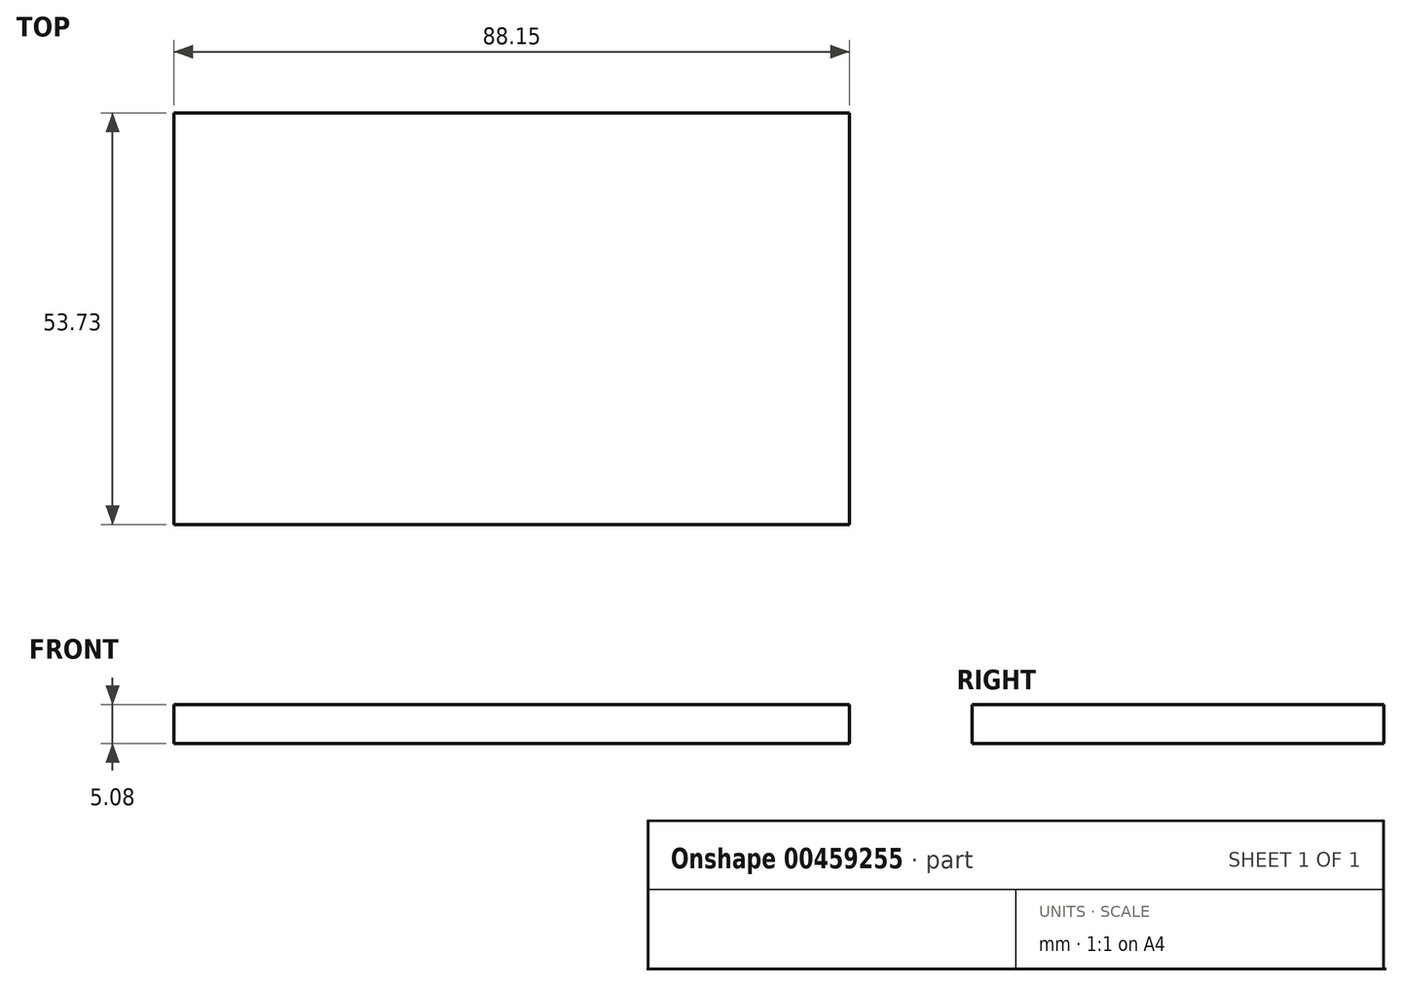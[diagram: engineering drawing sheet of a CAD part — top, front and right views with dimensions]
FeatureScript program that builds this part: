
annotation { "Feature Type Name" : "Feature", "Feature Type Description" : "" }
export const myFeature = defineFeature(function(context is Context, id is Id, definition is map)
    precondition{}
    {
        {
            var Q0;
            Q0=qCreatedBy(makeId("Top.planeOp"),FACE);
            var sketch = newSketch(context, id + "F0", { "sketchPlane" : qUnion([Q0])});
            skLineSegment(sketch, "E0.bottom", {"start": v(-24.19, 15.82) * mm, "end": v(63.96, 15.82) * mm});
            skLineSegment(sketch, "E0.top", {"start": v(-24.19, -37.91) * mm, "end": v(63.96, -37.91) * mm});
            skLineSegment(sketch, "E0.left", {"start": v(-24.19, 15.82) * mm, "end": v(-24.19, -37.91) * mm});
            skLineSegment(sketch, "E0.right", {"start": v(63.96, 15.82) * mm, "end": v(63.96, -37.91) * mm});
            skSolve(sketch);
        }
        {
            var Q0;
            Q0=makeQuery(id+"F0.imprint","IMPRINT",FACE,{"disambiguationData":[TD([[makeQuery(id+"F0.imprint","IMPRINT",EDGE,{"derivedFrom":sQuery(id+"F0.wireOp",EDGE,"E0.bottom")}),-1.0]])]});
            extrude(context, id + "F1", {"entities" : qUnion([Q0]), "depth" : 5.08 * mm});
        }
    });
